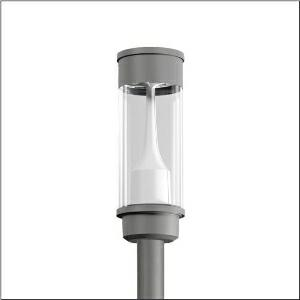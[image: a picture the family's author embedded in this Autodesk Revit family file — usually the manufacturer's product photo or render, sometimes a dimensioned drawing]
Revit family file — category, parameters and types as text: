
# Revit family: litepole_iq___pl1_2s_5xa5415jf14h000022_dba0
name_source: partatom
category: Lighting Fixtures
units: mm (PartAtom-declared; Revit-internal decimal feet)

## family parameters
Cut with Voids When Loaded = No
Host = Face
Light Source = No
Part Type = Normal
Room Calculation Point = No
Round Connector Dimension = Use Diameter
Shared = No

## types (1)
- --- (1 x LED, 2970 lm, 19.3 W, 3000K)
    Apparent Load = 19 VA
    CIE Flux Codes = 23 62 94 96 100
    Color Rendering = 70
    Color Temperature = 3000K
    Default Elevation = 1800 mm
    Description = Litepole iQ, mast luminaire, Module 540 iQ-SR, primary light control with 3 zone facetted reflector, of plastic, silver coated, highly specular, structured, primary optical cover: cover, of PMMA, transparent, light distribution: PL1.2s, light emission: direct distribution, primary light characteristic: symmetric, installation type: post-top, LED, High Power LED, rated luminous flux: 2.970lm, luminous efficacy: 154lm/W, light colour: 730, colour temperature: 3000K, control gear: iQ Street-Remote, control: Street-Remote, Auto-Match, Temp-Guard, Lumen-Switch, Night-Set, Smart-Wire, Light-Fading, Desk-Remote (wireless, voltage-free reading and setting of iQ features in the workshop via application-optimized NFC function/RFID function), optimised constant luminous flux control (CLO 2.0), pre-setting: logarithmic dimming characteristic, mains connection: 230..240V, AC, 50/60Hz, connection cable pre-assembled, cable length: 5,5m, wiring characteristics: H07RN-F, start of lifetime: 19W, end of service life: 21W, reduction: 10W, luminaire housing, upper part, of glass-fibre reinforced polyester, coated, Siteco® metallic grey (DB 702S), diameter: 210mm, height: 590mm, spigot size: d x l = 76 x 70mm (post-top) | with reducer (optional accessory) 60 x 70mm, mounting height: 3..5m, post-top mast mounting element, of diecast aluminium, coated, Siteco® metallic grey (DB 702S), Module 540 iQ-SR, traffic white (RAL 9016), equipment: standard, protection rating (complete): IP65, insulation class (complete): insulation class II (safety insulation), certification: CE, ENEC, VDE, packaging unit: 1 piece

Light Distribution: PL1.2s
    Height = 590 mm
    Lamp = 1 x LED
    Lamp Light Flux = 2970 lm
    Lamp Power = 19.3 W
    Lamp count = 1
    Length = 220 mm
    Luminous efficacy = 154 lm/W
    Manufacturer = Siteco
    ModVariant = No
    Model = 5XA5415JF14H000022
    Number of Poles = 1
    OnlyDefault = Yes
    Power Factor = 1
    Product Name = Litepole iQ | PL1.2s
    Product group = mast luminaire | pylon top
    ProductGroupID = 6100
    Protection Class = Protection class II
    Protection Degree = IP 65
    RLX_Detail_Level = 1
    RLX_Emergency_Light_Flux = 0 lm
    RLX_Emergency_Type = 0
    RLX_Emergency_Type_DB = No
    RlxData = <blob elided: 25049 chars, md5=cdce6bdd>
    Socket = socket
    Standby Power = 0 W
    System Light Flux = 2970 lm
    System Power = 19 W
    Type Comments = factory setting: luminous flux: 100 % | dim-lin: 254 | 403 mA
    Type Image = l_1006025.jpg
    URL = http://relux.com
    VarID = @adj_166235
    Voltage = 0 V
    Weight = 0.00 kg
    Width = 0 mm  [stored 0 ft]

note: [stored X ft] marks values corroborated as IEEE doubles in the binary element streams (Revit-internal decimal feet)

## geometry (parser evidence)
native form markers: Blend x4, Sweep x10
no freeform markers — native parametric forms only
